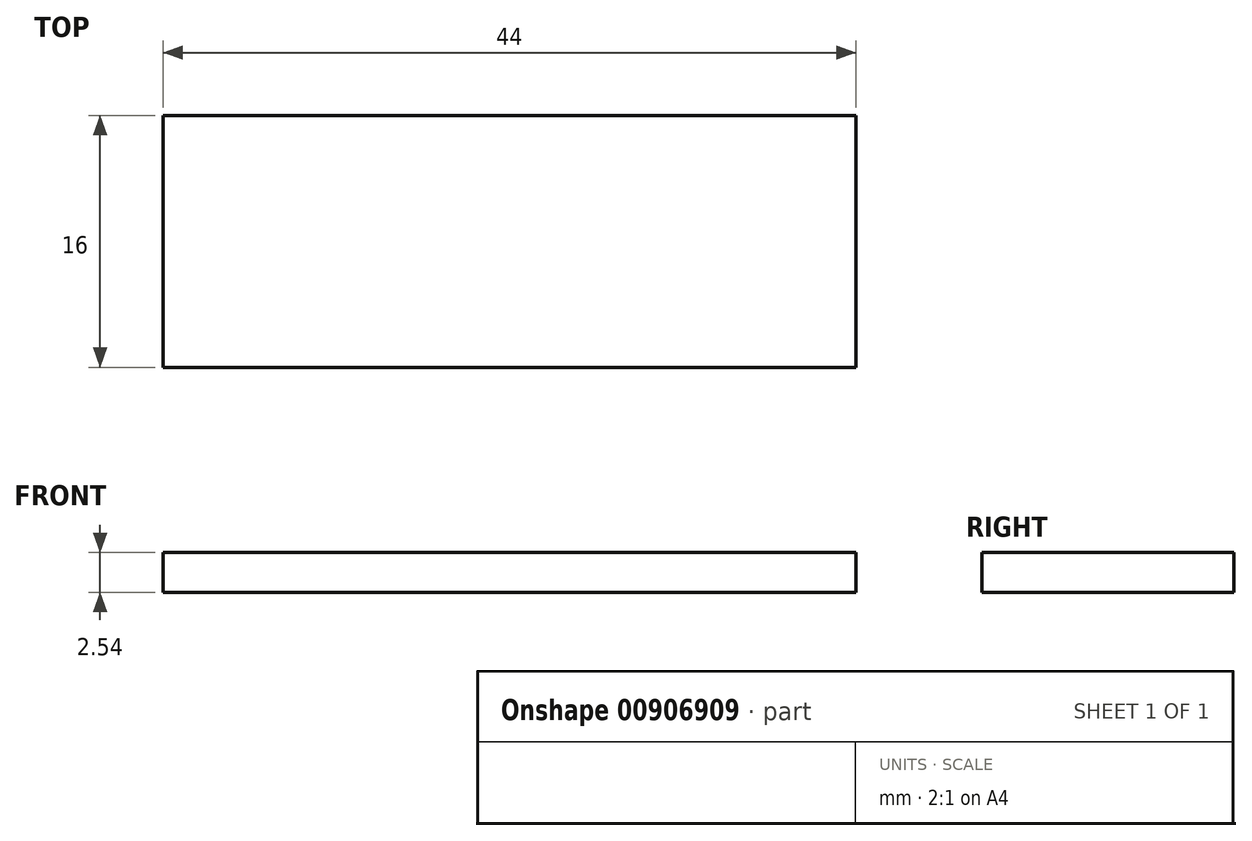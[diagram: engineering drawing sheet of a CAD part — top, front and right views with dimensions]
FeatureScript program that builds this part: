
annotation { "Feature Type Name" : "Feature", "Feature Type Description" : "" }
export const myFeature = defineFeature(function(context is Context, id is Id, definition is map)
    precondition{}
    {
        {
            var Q0;
            Q0=qCreatedBy(makeId("Top.planeOp"),FACE);
            var sketch = newSketch(context, id + "F0", { "sketchPlane" : qUnion([Q0])});
            skLineSegment(sketch, "E0.bottom", {"start": v(22, -8) * mm, "end": v(-22, -8) * mm});
            skLineSegment(sketch, "E0.top", {"start": v(22, 8) * mm, "end": v(-22, 8) * mm});
            skLineSegment(sketch, "E0.left", {"start": v(22, -8) * mm, "end": v(22, 8) * mm});
            skLineSegment(sketch, "E0.right", {"start": v(-22, -8) * mm, "end": v(-22, 8) * mm});
            skPoint(sketch, "E0.middle", {"position": v(0, 0) * mm});
            skSolve(sketch);
        }
        {
            var Q0;
            Q0=makeQuery(id+"F0.imprint","IMPRINT",FACE,{"disambiguationData":[TD([[makeQuery(id+"F0.imprint","IMPRINT",EDGE,{"derivedFrom":sQuery(id+"F0.wireOp",EDGE,"E0.bottom")}),-1.0]])]});
            extrude(context, id + "F1", {"entities" : qUnion([Q0]), "depth" : 2.54 * mm, "offsetDistance" : 25.4 * mm});
        }
    });
